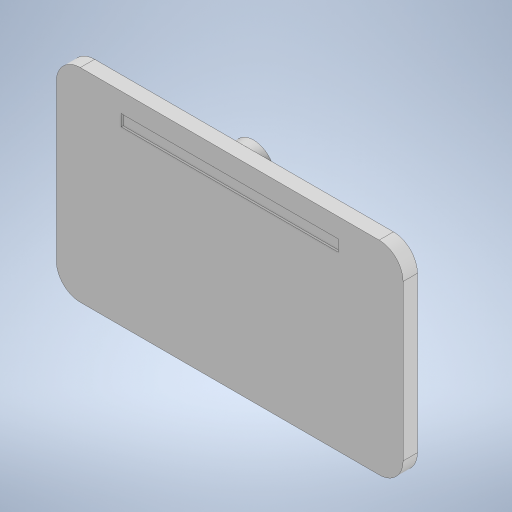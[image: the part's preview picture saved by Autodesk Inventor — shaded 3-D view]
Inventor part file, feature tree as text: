
AUTODESK INVENTOR PART (.ipt)
format: ipt  version: 2023 (Build 270158000, 158)  size: 317,952 bytes
history: native  units: mm
features: extrude x6, sketch x6, projected_geometry x3, other x2, fillet x2, chamfer x2, mirror x2
ambient origin geometry x8: Origin, YZ Plane, XZ Plane, XY Plane, X Axis, Y Axis, Z Axis, Center Point
bodies: Body1 (feature_tree)
feature tree (23):
  other  "솔리드1"
  extrude  "돌출1"  Depth=72.5mm
  extrude  "돌출2"  Depth=42.5mm
  fillet  "모깎기1"  Radius=3.0mm
  extrude  "돌출4"  Depth=4.5mm
  chamfer  "모따기1"  Distance=4.5mm
  other  "작업 평면1"
  extrude  "돌출5"  Depth=16.825mm
  mirror  "미러1"
  fillet  "모깎기2"  Radius=2.0mm
  extrude  "돌출6"  Depth=5.0mm
  extrude  "돌출7"  Depth=2.0mm
  chamfer  "모따기2"  Distance=45.0mm
  mirror  "미러2"
  sketch  "스케치1"
  sketch  "스케치2"
  projected_geometry  "투영된 루프1"
  sketch  "스케치5"
  sketch  "스케치6"
  sketch  "스케치7"
  projected_geometry  "투영된 루프3"
  projected_geometry  "투영된 루프4"
  sketch  "스케치8"
